# Revit family: g2021_EN_Roll-up-Door_Ferroflex_Self-Repairing-RS_D01418ES
name_source: partatom
category: Doors
units: mm (PartAtom-declared; Revit-internal decimal feet)

## family parameters
Always vertical = Yes
Cut with Voids When Loaded = No
Host = Wall
OmniClass Number = 23.30.10.00
OmniClass Title = Doors
Room Calculation Point = No
Shared = No

## types (1)
- Roll-up Door, 4000 x 4000 mm
    A = 275 mm
    Analytic Construction = <Ninguno>
    Antepecho Externo = No
    Antepecho Interno = No
    Article Number = D01418ES-V0
    Assembly Place = On site
    Atmospheric Acidification Per Unit = 0
    B = 285 mm  [stored 0.935039 ft]
    BIM Content Download Platform = www.bimetica.com
    BIM Eelement Expiry Date = 2 years
    BIM Element Issue Date = 29/11/2022
    BIM Profile URL = https://bimetica.com
    BIM technical support = https://bimsupport.info
    C = 480 mm  [stored 1.5748 ft]
    CE Mark = Yes
    COBie Category = IfcDoor
    Clear Area to Access = 0 mm  [stored 0 ft]
    Clear Height = 6000 mm  [stored 19.685 ft]
    Clear Width = 6000 mm  [stored 19.685 ft]
    Climate Change Per Unit = 0
    Code = Self-repairing RS
    Container Material = Wooden box
    Control panel Height = 1200 mm
    Curtain Material = PVC_Blue
    D = 100 mm  [stored 0.328084 ft]
    Declaration of Performance URL = https://ferroflexindustrialaccess.com
    Define Thermal Properties by = Schematic Type
    Description = Rapid roll-up door, consisting of guides and head in lacquered or anodized aluminum. PVC canvas with polyester fabric, color to choose. Control panel with variator. Active security by means of crossed photocells barriers.
    E = 60 mm  [stored 0.19685 ft]
    Energy Spent = 0
    Eutrophication Per Unit = 0
    Exterior Offset = 0 mm  [stored 0 ft]
    Finish = Estructura de hierro o Inox y lona de PVC
    Fire Rating = Curtain ISO 3795-89
    FireExit = No
    Frame Projection Ext. = 25 mm  [stored 0.082021 ft]
    Frame Projection Int. = 25 mm  [stored 0.082021 ft]
    Function = Exterior
    G = 380 mm
    GDO-BIM Standard Version = GDO-BIM V02
    Glazing Area Fraction = 0
    Gubimclass Code = Puertas de acceso
    Gubimclass Title = 80.10.40.20
    HasDrive = Yes
    Hazardous Waste Per Unit = 0
    Height = 4000 mm  [stored 13.1234 ft]
    History = (RVT2021) Creation of Element.
    IfcExportAs = IfcDoor
    IfcExportType = Roll-up door
    Inert Waste Per Unit = 0
    Infiltration = 0
    Interior Offset = 0 mm  [stored 0 ft]
    Is Accesible = No
    Is Extended Warranty = No
    Is External = Yes
    License Number = XXX-XXXX7125
    Maintenance Cost = 0
    Manufacturer = Ferroflex S.L.U.
    Masterformat Code = 08 31 00
    Masterformat Title = Access Doors and Panels
    Material = Stainless Steel_Laquered
    Measuring Unit = Unit
    Minimum Required Height = 2100 mm
    Model = Self-repairing RS
    Model Label = Self-repairing RS Roll-up Door
    Non Renewable Energy Consumption Per Unit = 0
    NonHazardous Waste Per Unit = 0
    Omniclass Code = 23-17 11 27 13
    Omniclass Title = Access Doors
    Operation = Enrrollable
    Photochemical Ozone Formation Per Unit = 0
    Product URL = https://ferroflexindustrialaccess.com
    Radioactive Waste Per Unit = 0
    Reference = D01418ES-V0
    Renewable Energy Consumption Per Unit = 0
    Resource Depletion Per Unit = 0
    Safety Standard = 2006/42/CE
    Security Rating = ISO 1421 / ISO 13937-2
    Self Closing = No
    Series = Roll-up Doors
    Sight glass area = Possibility of sight glass areas are available
    SmokeStop = No
    Stratospheric Ozone Layer Destruction Per Unit = 0
    Thickness = 60 mm  [stored 0.19685 ft]
    Total Primary Energy Consumption Per Unit = 0
    UNSPSC Code = 30171503
    UNSPSC Title = Rolling doors
    URL = https://ferroflexindustrialaccess.com
    Version = RVT2021
    Wall Closure = Interior
    Warranty Content = Materials
    Warranty Period = One year
    Water Consumption Per Unit = 0
    Weight = 0.00 kg
    Width = 4000 mm  [stored 13.1234 ft]
    Wind Load Rating = Clase 2
    Wrapping Material = Plastic wrapping

note: [stored X ft] marks values corroborated as IEEE doubles in the binary element streams (Revit-internal decimal feet)

## geometry (parser evidence)
native form markers: Sweep x3
no freeform markers — native parametric forms only
